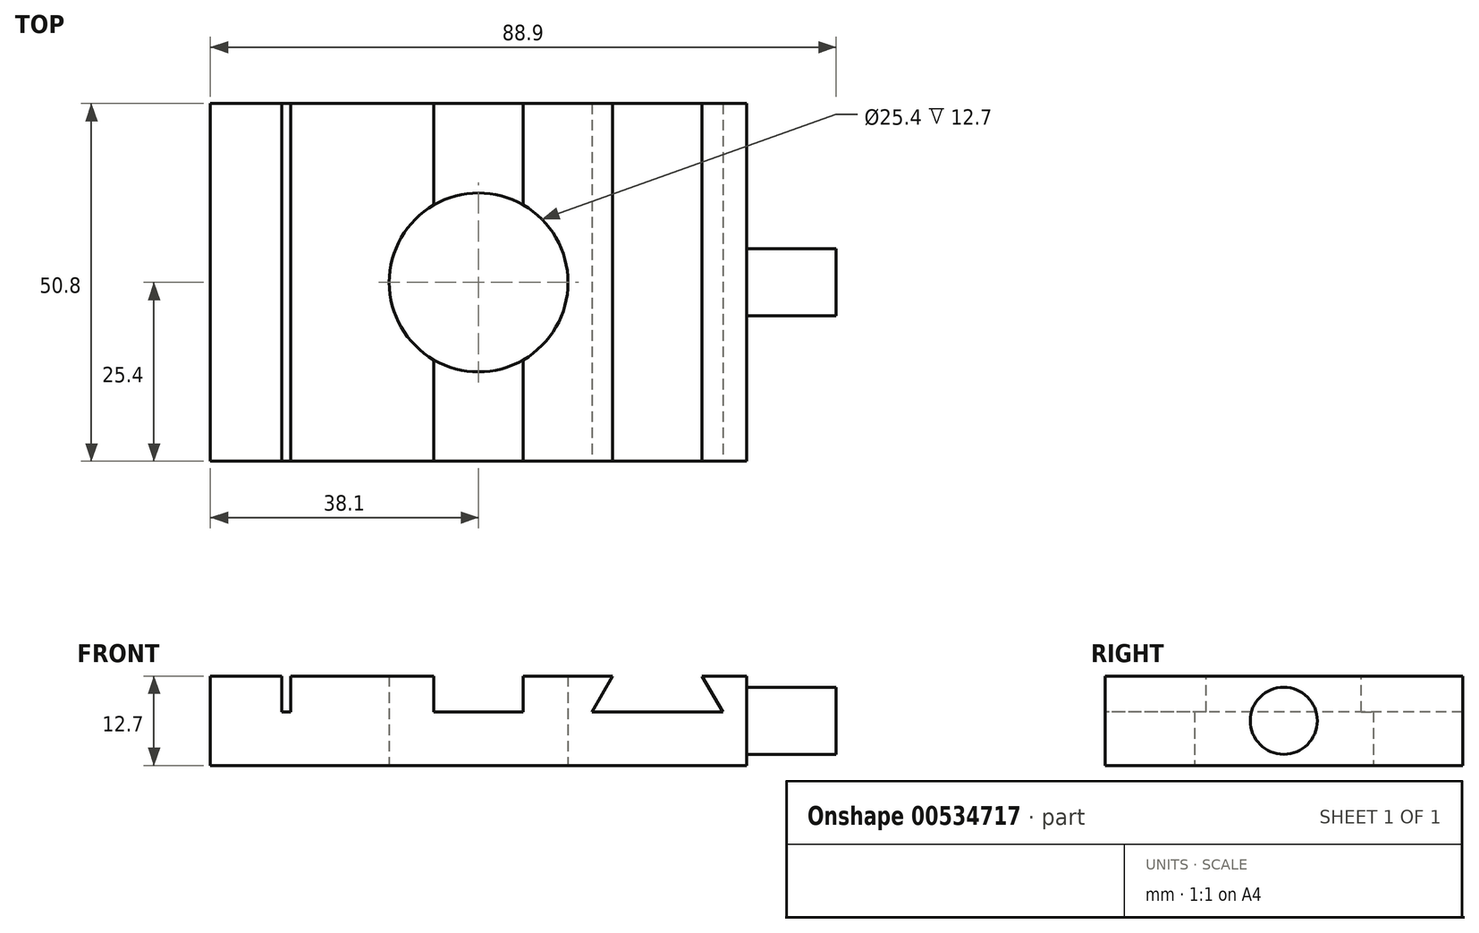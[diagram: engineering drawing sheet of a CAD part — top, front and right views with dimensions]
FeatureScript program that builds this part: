
annotation { "Feature Type Name" : "Feature", "Feature Type Description" : "" }
export const myFeature = defineFeature(function(context is Context, id is Id, definition is map)
    precondition{}
    {
        {
            var Q0;
            Q0=qCreatedBy(makeId("Top.planeOp"),FACE);
            var sketch = newSketch(context, id + "F0", { "sketchPlane" : qUnion([Q0])});
            skLineSegment(sketch, "E0.bottom", {"start": v(38.1, 25.4) * mm, "end": v(-38.1, 25.4) * mm});
            skLineSegment(sketch, "E0.top", {"start": v(38.1, -25.4) * mm, "end": v(-38.1, -25.4) * mm});
            skLineSegment(sketch, "E0.left", {"start": v(38.1, 25.4) * mm, "end": v(38.1, -25.4) * mm});
            skLineSegment(sketch, "E0.right", {"start": v(-38.1, 25.4) * mm, "end": v(-38.1, -25.4) * mm});
            skPoint(sketch, "E0.middle", {"position": v(0, 0) * mm});
            skCircle(sketch, "E1", {"center": v(0, 0) * mm, "radius": 12.7 * mm});
            skSolve(sketch);
        }
        {
            var Q0;
            Q0=makeQuery(id+"F0.imprint","IMPRINT",FACE,{"disambiguationData":[TD([[makeQuery(id+"F0.imprint","IMPRINT",EDGE,{"derivedFrom":sQuery(id+"F0.wireOp",EDGE,"E0.bottom")}),1.0]])]});
            extrude(context, id + "F1", {"entities" : qUnion([Q0]), "depth" : 12.7 * mm, "offsetDistance" : 25.4 * mm});
        }
        {
            var Q0;
            Q0=makeQuery(id+"F1.opExtrude","CAP_FACE",FACE,{"disambiguationData":[OSD([sQuery(id+"F0.wireOp",EDGE,"E0.bottom"),sQuery(id+"F0.wireOp",EDGE,"E0.top"),sQuery(id+"F0.wireOp",EDGE,"E0.left"),sQuery(id+"F0.wireOp",EDGE,"E0.right"),sQuery(id+"F0.wireOp",EDGE,"E1")])],"isStart":false});
            var sketch = newSketch(context, id + "F2", { "sketchPlane" : qUnion([Q0])});
            skLineSegment(sketch, "E2.bottom", {"start": v(-27.94, 25.4) * mm, "end": v(-26.67, 25.4) * mm});
            skLineSegment(sketch, "E2.top", {"start": v(-27.94, -25.4) * mm, "end": v(-26.67, -25.4) * mm});
            skLineSegment(sketch, "E2.left", {"start": v(-27.94, 25.4) * mm, "end": v(-27.94, -25.4) * mm});
            skLineSegment(sketch, "E2.right", {"start": v(-26.67, 25.4) * mm, "end": v(-26.67, -25.4) * mm});
            skLineSegment(sketch, "E3", {"start": v(-6.35, 25.4) * mm, "end": v(-6.35, -25.4) * mm});
            skLineSegment(sketch, "E4", {"start": v(-6.35, -25.4) * mm, "end": v(6.35, -25.4) * mm});
            skLineSegment(sketch, "E5", {"start": v(6.35, -25.4) * mm, "end": v(6.35, 25.4) * mm});
            skLineSegment(sketch, "E6", {"start": v(6.35, 25.4) * mm, "end": v(-6.35, 25.4) * mm});
            skPoint(sketch, "E7", {"position": v(0, 0) * mm});
            skLineSegment(sketch, "E8", {"start": v(0, 25.4) * mm, "end": v(0, -25.4) * mm, "construction": true});
            skSolve(sketch);
        }
        {
            var Q0;
            Q0=makeQuery(id+"F2.imprint","IMPRINT",FACE,{"disambiguationData":[TD([[makeQuery(id+"F2.imprint","IMPRINT",EDGE,{"derivedFrom":sQuery(id+"F2.wireOp",EDGE,"E2.bottom")}),1.0]])]});
            var Q1;
            {var subQ0=sQuery(id+"F2.wireOp",EDGE,"E4");Q1=makeQuery(id+"F2.imprint","IMPRINT",FACE,{"disambiguationData":[TD([[makeQuery(id+"F2.imprint","IMPRINT",EDGE,{"derivedFrom":subQ0}),-1.0]])]});}
            var Q2;
            {var subQ0=sQuery(id+"F2.wireOp",EDGE,"E6");Q2=makeQuery(id+"F2.imprint","IMPRINT",FACE,{"disambiguationData":[TD([[makeQuery(id+"F2.imprint","IMPRINT",EDGE,{"derivedFrom":subQ0}),1.0]])]});}
            extrude(context, id + "F3", {"entities" : qUnion([Q0, Q1, Q2]), "operationType" : NewBodyOperationType.REMOVE, "oppositeDirection" : true, "depth" : 5.08 * mm, "offsetDistance" : 25.4 * mm});
        }
        {
            var Q0;
            Q0=makeQuery(id+"F1.opExtrude","SWEPT_FACE",FACE,{"disambiguationData":[OSD([sQuery(id+"F0.wireOp",EDGE,"E0.top")])]});
            var sketch = newSketch(context, id + "F4", { "sketchPlane" : qUnion([Q0])});
            skLineSegment(sketch, "E9", {"start": v(19.05, 12.7) * mm, "end": v(16.12, 7.62) * mm});
            skLineSegment(sketch, "E10", {"start": v(16.12, 7.62) * mm, "end": v(34.68, 7.62) * mm});
            skLineSegment(sketch, "E11", {"start": v(34.68, 7.62) * mm, "end": v(31.75, 12.7) * mm});
            skLineSegment(sketch, "E12", {"start": v(31.75, 12.7) * mm, "end": v(19.05, 12.7) * mm});
            skLineSegment(sketch, "E13", {"start": v(25.4, 7.62) * mm, "end": v(25.4, 12.7) * mm, "construction": true});
            skSolve(sketch);
        }
        {
            var Q0;
            Q0=makeQuery(id+"F4.imprint","IMPRINT",FACE,{"disambiguationData":[TD([[makeQuery(id+"F4.imprint","IMPRINT",EDGE,{"derivedFrom":sQuery(id+"F4.wireOp",EDGE,"E9")}),1.0]])]});
            extrude(context, id + "F5", {"entities" : qUnion([Q0]), "operationType" : NewBodyOperationType.REMOVE, "endBound" : BoundingType.THROUGH_ALL, "oppositeDirection" : true, "depth" : 25.4 * mm, "offsetDistance" : 25.4 * mm});
        }
        {
            var Q0;
            Q0=makeQuery(id+"F1.opExtrude","SWEPT_FACE",FACE,{"disambiguationData":[OSD([sQuery(id+"F0.wireOp",EDGE,"E0.left")])]});
            var sketch = newSketch(context, id + "F6", { "sketchPlane" : qUnion([Q0])});
            skCircle(sketch, "E14", {"center": v(0, 6.35) * mm, "radius": 4.76 * mm});
            skPoint(sketch, "E14.centerSnap0", {"position": v(-25.4, 6.35) * mm});
            skPoint(sketch, "E14.centerSnap1", {"position": v(0, 12.7) * mm});
            skSolve(sketch);
        }
        {
            var Q0;
            Q0=makeQuery(id+"F6.imprint","IMPRINT",FACE,{"disambiguationData":[TD([[makeQuery(id+"F6.imprint","IMPRINT",EDGE,{"derivedFrom":sQuery(id+"F6.wireOp",EDGE,"E14")}),1.0]])]});
            extrude(context, id + "F7", {"entities" : qUnion([Q0]), "operationType" : NewBodyOperationType.ADD, "depth" : 12.7 * mm, "offsetDistance" : 25.4 * mm});
        }
    });
